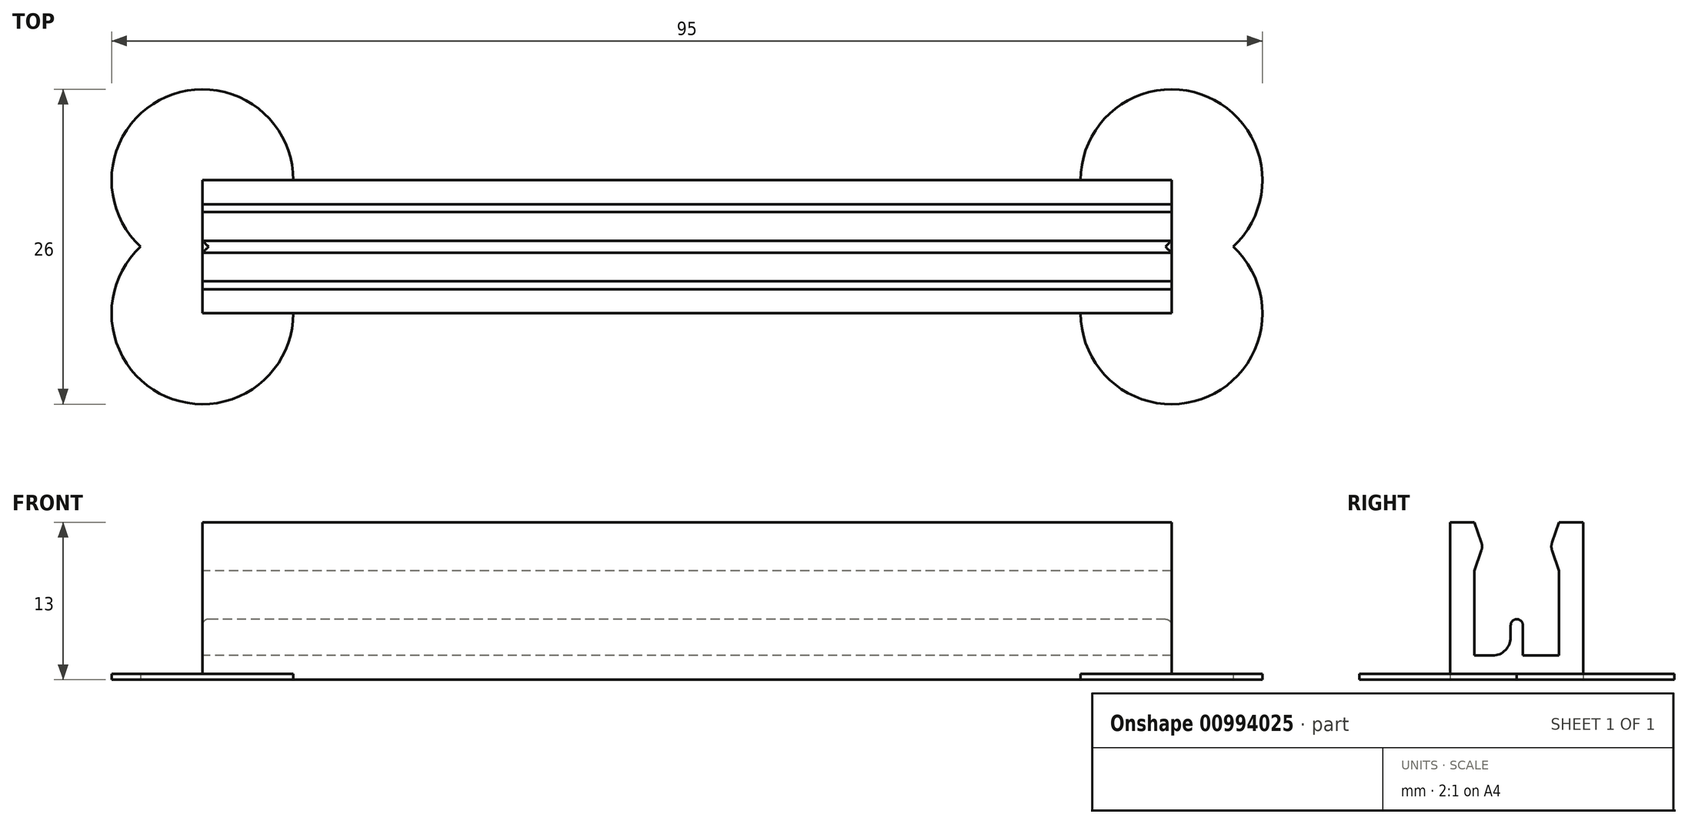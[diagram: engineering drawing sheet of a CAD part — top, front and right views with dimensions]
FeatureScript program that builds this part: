
annotation { "Feature Type Name" : "Feature", "Feature Type Description" : "" }
export const myFeature = defineFeature(function(context is Context, id is Id, definition is map)
    precondition{}
    {
        {
            var Q0;
            Q0=qCreatedBy(makeId("Top.planeOp"),FACE);
            var sketch = newSketch(context, id + "F0", { "sketchPlane" : qUnion([Q0])});
            skLineSegment(sketch, "E0.bottom", {"start": v(40, 5.5) * mm, "end": v(-40, 5.5) * mm});
            skLineSegment(sketch, "E0.top", {"start": v(40, -5.5) * mm, "end": v(-40, -5.5) * mm});
            skLineSegment(sketch, "E0.left", {"start": v(40, 5.5) * mm, "end": v(40, -5.5) * mm});
            skLineSegment(sketch, "E0.right", {"start": v(-40, 5.5) * mm, "end": v(-40, -5.5) * mm});
            skPoint(sketch, "E0.middle", {"position": v(0, 0) * mm});
            skLineSegment(sketch, "E1.bottom", {"start": v(-40, 5.5) * mm, "end": v(40, 5.5) * mm});
            skLineSegment(sketch, "E1.top", {"start": v(-40, 3.5) * mm, "end": v(40, 3.5) * mm});
            skLineSegment(sketch, "E1.left", {"start": v(-40, 5.5) * mm, "end": v(-40, 3.5) * mm});
            skLineSegment(sketch, "E1.right", {"start": v(40, 5.5) * mm, "end": v(40, 3.5) * mm});
            skLineSegment(sketch, "E2.bottom", {"start": v(-40, -5.5) * mm, "end": v(40, -5.5) * mm});
            skLineSegment(sketch, "E2.top", {"start": v(-40, -3.5) * mm, "end": v(40, -3.5) * mm});
            skLineSegment(sketch, "E2.left", {"start": v(-40, -5.5) * mm, "end": v(-40, -3.5) * mm});
            skLineSegment(sketch, "E2.right", {"start": v(40, -5.5) * mm, "end": v(40, -3.5) * mm});
            skSolve(sketch);
        }
        {
            var Q0;
            {var subQ0=sQuery(id+"F0.wireOp",EDGE,"E1.top");Q0=makeQuery(id+"F0.imprint","IMPRINT",FACE,{"disambiguationData":[TD([[makeQuery(id+"F0.imprint","IMPRINT",EDGE,{"derivedFrom":subQ0}),-1.0]])]});}
            extrude(context, id + "F1", {"entities" : qUnion([Q0]), "depth" : 2 * mm, "offsetDistance" : 25 * mm});
        }
        {
            var Q0;
            {var subQ0=sQuery(id+"F0.wireOp",EDGE,"E0.bottom");Q0=makeQuery(id+"F0.imprint","IMPRINT",FACE,{"disambiguationData":[TD([[makeQuery(id+"F0.imprint","IMPRINT",EDGE,{"derivedFrom":subQ0}),1.0]])]});}
            var Q1;
            {var subQ0=sQuery(id+"F0.wireOp",EDGE,"E0.top");Q1=makeQuery(id+"F0.imprint","IMPRINT",FACE,{"disambiguationData":[TD([[makeQuery(id+"F0.imprint","IMPRINT",EDGE,{"derivedFrom":subQ0}),-1.0]])]});}
            extrude(context, id + "F2", {"entities" : qUnion([Q0, Q1]), "operationType" : NewBodyOperationType.ADD, "depth" : 13 * mm, "offsetDistance" : 25 * mm});
        }
        {
            var Q0;
            {var subQ0=sQuery(id+"F0.wireOp",EDGE,"E0.right");Q0=makeQuery(id+"F2.boolean.opBoolean","MERGE",FACE,{"derivedFrom":[makeQuery(id+"F1.opExtrude","SWEPT_FACE",FACE,{"disambiguationData":[OSD([subQ0])]}),makeQuery(id+"F2.opExtrude","SWEPT_FACE",FACE,{"disambiguationData":[OSD([subQ0]),TDD([makeQuery(id+"F0.imprint","IMPRINT",EDGE,{"disambiguationData":[TD([[makeQuery(id+"F0.imprint","INTERSECT",VERTEX,{"derivedFrom":[sQuery(id+"F0.wireOp",EDGE,"E0.bottom"),subQ0]}),-1.0]])],"derivedFrom":subQ0})])]}),makeQuery(id+"F2.opExtrude","SWEPT_FACE",FACE,{"disambiguationData":[OSD([subQ0]),TDD([makeQuery(id+"F0.imprint","IMPRINT",EDGE,{"disambiguationData":[TD([[makeQuery(id+"F0.imprint","INTERSECT",VERTEX,{"derivedFrom":[sQuery(id+"F0.wireOp",EDGE,"E0.top"),subQ0]}),1.0]])],"derivedFrom":subQ0})])]})]});}
            var sketch = newSketch(context, id + "F3", { "sketchPlane" : qUnion([Q0])});
            skLineSegment(sketch, "E3.bottom", {"start": v(-5.5, 13) * mm, "end": v(5.5, 13) * mm, "construction": true});
            skLineSegment(sketch, "E3.top", {"start": v(-5.5, 9) * mm, "end": v(5.5, 9) * mm, "construction": true});
            skLineSegment(sketch, "E3.left", {"start": v(-5.5, 13) * mm, "end": v(-5.5, 9) * mm, "construction": true});
            skLineSegment(sketch, "E3.right", {"start": v(5.5, 13) * mm, "end": v(5.5, 9) * mm, "construction": true});
            skLineSegment(sketch, "E4.bottom", {"start": v(-3.5, 13) * mm, "end": v(-2.8, 13) * mm, "construction": true});
            skLineSegment(sketch, "E4.top", {"start": v(-3.5, 9) * mm, "end": v(-2.8, 9) * mm, "construction": true});
            skLineSegment(sketch, "E4.left", {"start": v(-3.5, 13) * mm, "end": v(-3.5, 9) * mm, "construction": true});
            skLineSegment(sketch, "E4.right", {"start": v(-2.8, 13) * mm, "end": v(-2.8, 9) * mm, "construction": true});
            skLineSegment(sketch, "E5.top", {"start": v(3.5, 13) * mm, "end": v(2.8, 13) * mm, "construction": true});
            skLineSegment(sketch, "E5.left", {"start": v(3.5, 7.5) * mm, "end": v(3.5, 13) * mm, "construction": true});
            skLineSegment(sketch, "E6.bottom", {"start": v(-3.5, 13) * mm, "end": v(3.5, 13) * mm, "construction": true});
            skLineSegment(sketch, "E6.left", {"start": v(-3.5, 13) * mm, "end": v(-3.5, 10.25) * mm, "construction": true});
            skLineSegment(sketch, "E6.right", {"start": v(3.5, 13) * mm, "end": v(3.5, 10.25) * mm, "construction": true});
            skLineSegment(sketch, "E7", {"start": v(-3.5, 9) * mm, "end": v(-2.8, 11) * mm});
            skLineSegment(sketch, "E8", {"start": v(-2.8, 11) * mm, "end": v(-3.5, 13) * mm});
            skLineSegment(sketch, "E9.top", {"start": v(-3.5, 11) * mm, "end": v(3.5, 11) * mm, "construction": true});
            skLineSegment(sketch, "E9.left", {"start": v(-3.5, 13) * mm, "end": v(-3.5, 11) * mm, "construction": true});
            skLineSegment(sketch, "E9.right", {"start": v(3.5, 13) * mm, "end": v(3.5, 11) * mm, "construction": true});
            skLineSegment(sketch, "E10.top", {"start": v(3.5, 9) * mm, "end": v(2.8, 9) * mm, "construction": true});
            skLineSegment(sketch, "E10.left", {"start": v(3.5, 13) * mm, "end": v(3.5, 9) * mm, "construction": true});
            skLineSegment(sketch, "E10.right", {"start": v(2.8, 13) * mm, "end": v(2.8, 9) * mm, "construction": true});
            skLineSegment(sketch, "E11", {"start": v(3.5, 9) * mm, "end": v(2.8, 11) * mm});
            skLineSegment(sketch, "E12", {"start": v(2.8, 11) * mm, "end": v(3.5, 13) * mm});
            skLineSegment(sketch, "E13.bottom", {"start": v(-0.5, 2) * mm, "end": v(0.5, 2) * mm});
            skLineSegment(sketch, "E13.top", {"start": v(-0.5, 5) * mm, "end": v(0.5, 5) * mm});
            skLineSegment(sketch, "E13.left", {"start": v(-0.5, 2) * mm, "end": v(-0.5, 5) * mm});
            skLineSegment(sketch, "E13.right", {"start": v(0.5, 2) * mm, "end": v(0.5, 5) * mm});
            skSolve(sketch);
        }
        {
            var Q0;
            {var subQ0=sQuery(id+"F3.wireOp",EDGE,"E7");Q0=makeQuery(id+"F3.imprint","IMPRINT",FACE,{"disambiguationData":[TD([[makeQuery(id+"F3.imprint","IMPRINT",EDGE,{"derivedFrom":subQ0}),1.0]])]});}
            var Q1;
            {var subQ0=sQuery(id+"F3.wireOp",EDGE,"JF0y7yOE-hZ0c-IGpq-qxWO-KcFmzZiD7cJA");Q1=makeQuery(id+"F3.imprint","IMPRINT",FACE,{"disambiguationData":[TD([[makeQuery(id+"F3.imprint","IMPRINT",EDGE,{"derivedFrom":subQ0}),-1.0]])]});}
            var Q2;
            {var subQ0=sQuery(id+"F3.wireOp",EDGE,"E11");Q2=makeQuery(id+"F3.imprint","IMPRINT",FACE,{"disambiguationData":[TD([[makeQuery(id+"F3.imprint","IMPRINT",EDGE,{"derivedFrom":subQ0}),-1.0]])]});}
            var Q3;
            Q3=makeQuery(id+"F3.imprint","IMPRINT",FACE,{"disambiguationData":[TD([[makeQuery(id+"F3.imprint","IMPRINT",EDGE,{"derivedFrom":sQuery(id+"F3.wireOp",EDGE,"E13.bottom")}),1.0]])]});
            extrude(context, id + "F4", {"entities" : qUnion([Q0, Q1, Q2, Q3]), "operationType" : NewBodyOperationType.ADD, "depth" : -80 * mm, "offsetDistance" : 25 * mm});
        }
        {
            var Q0;
            Q0=makeQuery(id+"F4.opExtrude","SWEPT_EDGE",EDGE,{"disambiguationData":[OSD([sQuery(id+"F3.wireOp",EDGE,"E7"),sQuery(id+"F3.wireOp",EDGE,"E8")])]});
            fillet(context, id + "F5", {"entities" : qUnion([Q0]), "radius" : 1 * mm, "tangentPropagation" : true, "allowEdgeOverflow" : false});
        }
        {
            var Q0;
            Q0=makeQuery(id+"F4.opExtrude","SWEPT_EDGE",EDGE,{"disambiguationData":[OSD([sQuery(id+"F3.wireOp",EDGE,"E11"),sQuery(id+"F3.wireOp",EDGE,"E12")])]});
            fillet(context, id + "F6", {"entities" : qUnion([Q0]), "radius" : 1 * mm, "tangentPropagation" : true, "allowEdgeOverflow" : false});
        }
        {
            var Q0;
            Q0=makeQuery(id+"F1.opExtrude","CAP_EDGE",EDGE,{"disambiguationData":[OSD([sQuery(id+"F0.wireOp",EDGE,"E2.top")])],"isStart":false});
            var Q1;
            Q1=makeQuery(id+"F1.opExtrude","CAP_EDGE",EDGE,{"disambiguationData":[OSD([sQuery(id+"F0.wireOp",EDGE,"E1.top")])],"isStart":false});
            var Q2;
            Q2=makeQuery(id+"F4.opExtrude","SWEPT_EDGE",EDGE,{"disambiguationData":[OSD([sQuery(id+"F0.wireOp",EDGE,"E0.right"),sQuery(id+"F3.wireOp",EDGE,"E13.bottom"),sQuery(id+"F3.wireOp",EDGE,"E13.right")])]});
            var Q3;
            Q3=makeQuery(id+"F4.opExtrude","SWEPT_EDGE",EDGE,{"disambiguationData":[OSD([sQuery(id+"F0.wireOp",EDGE,"E0.right"),sQuery(id+"F3.wireOp",EDGE,"E13.bottom"),sQuery(id+"F3.wireOp",EDGE,"E13.left")])]});
            fillet(context, id + "F7", {"entities" : qUnion([Q0, Q1, Q2, Q3]), "radius" : 1.5 * mm, "tangentPropagation" : true, "allowEdgeOverflow" : false});
        }
        {
            var Q0;
            Q0=makeQuery(id+"F4.opExtrude","SWEPT_FACE",FACE,{"disambiguationData":[OSD([sQuery(id+"F3.wireOp",EDGE,"E13.top")])]});
            var Q1;
            Q1=makeQuery(id+"F4.opExtrude","SWEPT_EDGE",EDGE,{"disambiguationData":[OSD([sQuery(id+"F3.wireOp",EDGE,"E13.top"),sQuery(id+"F3.wireOp",EDGE,"E13.left")])]});
            fillet(context, id + "F8", {"entities" : qUnion([Q0, Q1]), "radius" : 0.5 * mm, "tangentPropagation" : true, "allowEdgeOverflow" : false});
        }
        {
            var Q0;
            {var subQ0=sQuery(id+"F0.wireOp",EDGE,"E2.top");var subQ1=sQuery(id+"F0.wireOp",EDGE,"E0.right");var subQ2=sQuery(id+"F0.wireOp",EDGE,"E0.left");var subQ3=sQuery(id+"F0.wireOp",EDGE,"E1.top");Q0=makeQuery(id+"F2.boolean.opBoolean","MERGE",FACE,{"derivedFrom":[makeQuery(id+"F1.opExtrude","CAP_FACE",FACE,{"disambiguationData":[OSD([subQ2,subQ1,subQ3,subQ0])],"isStart":true}),makeQuery(id+"F2.opExtrude","CAP_FACE",FACE,{"disambiguationData":[OSD([sQuery(id+"F0.wireOp",EDGE,"E0.bottom"),subQ2,subQ1,subQ3])],"isStart":true}),makeQuery(id+"F2.opExtrude","CAP_FACE",FACE,{"disambiguationData":[OSD([sQuery(id+"F0.wireOp",EDGE,"E0.top"),subQ2,subQ1,subQ0])],"isStart":true})]});}
            var sketch = newSketch(context, id + "F9", { "sketchPlane" : qUnion([Q0])});
            skCircle(sketch, "E14", {"center": v(-40, 5.5) * mm, "radius": 7.5 * mm});
            skCircle(sketch, "E15", {"center": v(-40, -5.5) * mm, "radius": 7.5 * mm});
            skCircle(sketch, "E16", {"center": v(40, 5.5) * mm, "radius": 7.5 * mm});
            skCircle(sketch, "E17", {"center": v(40, -5.5) * mm, "radius": 7.5 * mm});
            skSolve(sketch);
        }
        {
            var Q0;
            {var subQ0=sQuery(id+"F9.wireOp",EDGE,"E15");var subQ1=sQuery(id+"F9.wireOp",EDGE,"E14");var subQ2=makeQuery(id+"F9.imprint","INTERSECT",VERTEX,{"disambiguationData":[OD(0.0)],"derivedFrom":[subQ1,subQ0]});Q0=makeQuery(id+"F9.imprint","IMPRINT",FACE,{"disambiguationData":[TD([[makeQuery(id+"F9.imprint","IMPRINT",EDGE,{"disambiguationData":[TD([[subQ2,-1.0]])],"derivedFrom":subQ1}),1.0]])]});}
            var Q1;
            {var subQ0=sQuery(id+"F9.wireOp",EDGE,"E15");var subQ1=sQuery(id+"F9.wireOp",EDGE,"E14");var subQ2=makeQuery(id+"F9.imprint","INTERSECT",VERTEX,{"disambiguationData":[OD(0.0)],"derivedFrom":[subQ1,subQ0]});Q1=makeQuery(id+"F9.imprint","IMPRINT",FACE,{"disambiguationData":[TD([[makeQuery(id+"F9.imprint","IMPRINT",EDGE,{"disambiguationData":[TD([[subQ2,1.0]])],"derivedFrom":subQ1}),1.0]])]});}
            var Q2;
            {var subQ0=sQuery(id+"F9.wireOp",EDGE,"E15");var subQ1=sQuery(id+"F9.wireOp",EDGE,"E14");var subQ2=makeQuery(id+"F9.imprint","INTERSECT",VERTEX,{"disambiguationData":[OD(0.0)],"derivedFrom":[subQ1,subQ0]});Q2=makeQuery(id+"F9.imprint","IMPRINT",FACE,{"disambiguationData":[TD([[makeQuery(id+"F9.imprint","IMPRINT",EDGE,{"disambiguationData":[TD([[subQ2,-1.0]])],"derivedFrom":subQ0}),1.0]])]});}
            var Q3;
            {var subQ0=sQuery(id+"F9.wireOp",EDGE,"E17");var subQ1=sQuery(id+"F9.wireOp",EDGE,"E16");var subQ2=makeQuery(id+"F9.imprint","INTERSECT",VERTEX,{"disambiguationData":[OD(0.0)],"derivedFrom":[subQ1,subQ0]});Q3=makeQuery(id+"F9.imprint","IMPRINT",FACE,{"disambiguationData":[TD([[makeQuery(id+"F9.imprint","IMPRINT",EDGE,{"disambiguationData":[TD([[subQ2,1.0]])],"derivedFrom":subQ0}),1.0]])]});}
            var Q4;
            {var subQ0=sQuery(id+"F9.wireOp",EDGE,"E17");var subQ1=sQuery(id+"F9.wireOp",EDGE,"E16");var subQ2=makeQuery(id+"F9.imprint","INTERSECT",VERTEX,{"disambiguationData":[OD(0.0)],"derivedFrom":[subQ1,subQ0]});Q4=makeQuery(id+"F9.imprint","IMPRINT",FACE,{"disambiguationData":[TD([[makeQuery(id+"F9.imprint","IMPRINT",EDGE,{"disambiguationData":[TD([[subQ2,1.0]])],"derivedFrom":subQ1}),1.0]])]});}
            var Q5;
            {var subQ0=sQuery(id+"F9.wireOp",EDGE,"E17");var subQ1=sQuery(id+"F9.wireOp",EDGE,"E16");var subQ2=makeQuery(id+"F9.imprint","INTERSECT",VERTEX,{"disambiguationData":[OD(0.0)],"derivedFrom":[subQ1,subQ0]});Q5=makeQuery(id+"F9.imprint","IMPRINT",FACE,{"disambiguationData":[TD([[makeQuery(id+"F9.imprint","IMPRINT",EDGE,{"disambiguationData":[TD([[subQ2,-1.0]])],"derivedFrom":subQ1}),1.0]])]});}
            extrude(context, id + "F10", {"entities" : qUnion([Q0, Q1, Q2, Q3, Q4, Q5]), "operationType" : NewBodyOperationType.ADD, "oppositeDirection" : true, "depth" : 0.5 * mm, "offsetDistance" : 25 * mm});
        }
    });
